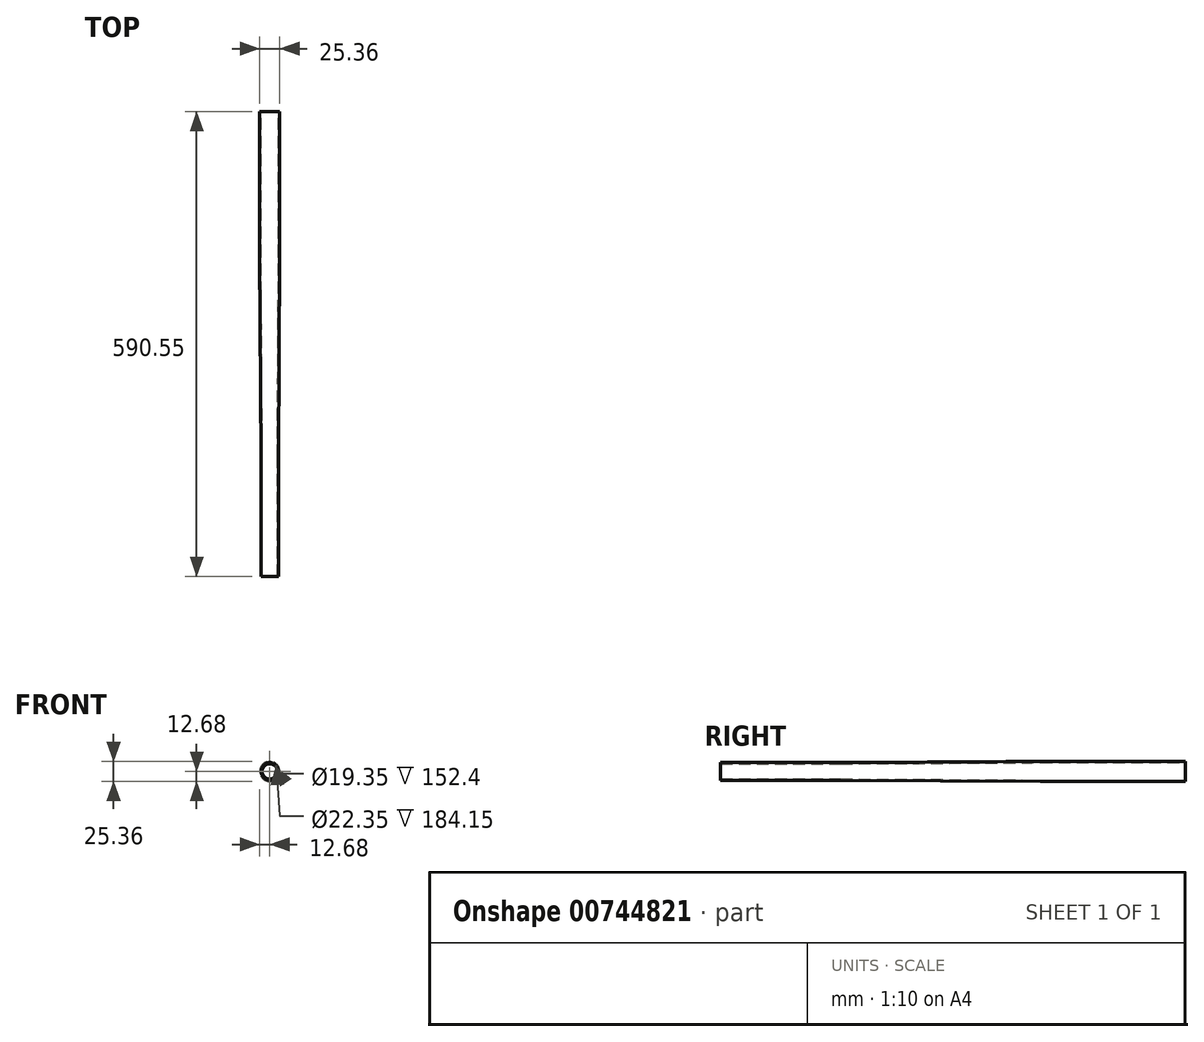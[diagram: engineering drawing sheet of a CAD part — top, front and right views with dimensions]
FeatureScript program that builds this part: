
annotation { "Feature Type Name" : "Feature", "Feature Type Description" : "" }
export const myFeature = defineFeature(function(context is Context, id is Id, definition is map)
    precondition{}
    {
        {
            var Q0;
            Q0=qCreatedBy(makeId("Right.planeOp"),FACE);
            var sketch = newSketch(context, id + "F0", { "sketchPlane" : qUnion([Q0])});
            skLineSegment(sketch, "E0", {"start": v(0, 0) * mm, "end": v(-19.05, 0) * mm});
            skLineSegment(sketch, "E1", {"start": v(-19.05, 0) * mm, "end": v(-184.15, 0) * mm});
            skLineSegment(sketch, "E2", {"start": v(-184.15, 0) * mm, "end": v(-438.15, 0) * mm});
            skLineSegment(sketch, "E3", {"start": v(-438.15, 0) * mm, "end": v(-590.55, 0) * mm});
            skLineSegment(sketch, "E4", {"start": v(0, 12.68) * mm, "end": v(-184.15, 12.68) * mm});
            skLineSegment(sketch, "E5", {"start": v(0, -14.92) * mm, "end": v(-184.15, -14.92) * mm});
            skLineSegment(sketch, "E6", {"start": v(-438.15, 11.18) * mm, "end": v(-590.55, 11.18) * mm});
            skLineSegment(sketch, "E7", {"start": v(-438.15, -11.18) * mm, "end": v(-590.55, -11.18) * mm});
            skLineSegment(sketch, "E8", {"start": v(-184.15, 12.68) * mm, "end": v(-438.15, 11.18) * mm});
            skLineSegment(sketch, "E9", {"start": v(-438.15, -11.18) * mm, "end": v(-184.15, -14.92) * mm});
            skLineSegment(sketch, "E10", {"start": v(-590.55, 11.18) * mm, "end": v(-590.55, 9.68) * mm});
            skLineSegment(sketch, "E11", {"start": v(-590.55, -11.18) * mm, "end": v(-590.55, -9.68) * mm});
            skLineSegment(sketch, "E12", {"start": v(-590.55, -9.68) * mm, "end": v(-438.15, -9.68) * mm});
            skLineSegment(sketch, "E13", {"start": v(-590.55, 9.68) * mm, "end": v(-438.15, 9.68) * mm});
            skLineSegment(sketch, "E14", {"start": v(0, 12.68) * mm, "end": v(0, 11.18) * mm});
            skLineSegment(sketch, "E15", {"start": v(0, -14.92) * mm, "end": v(0, -13.42) * mm});
            skLineSegment(sketch, "E16", {"start": v(0, 11.18) * mm, "end": v(-184.15, 11.18) * mm});
            skLineSegment(sketch, "E17", {"start": v(0, -13.42) * mm, "end": v(-184.15, -13.42) * mm});
            skLineSegment(sketch, "E18", {"start": v(-184.15, 11.18) * mm, "end": v(-438.15, 9.68) * mm});
            skLineSegment(sketch, "E19", {"start": v(-184.15, -13.42) * mm, "end": v(-438.15, -9.68) * mm});
            skSolve(sketch);
        }
        {
            var Q0;
            Q0=makeQuery(id+"F0.imprint","IMPRINT",FACE,{"disambiguationData":[TD([[makeQuery(id+"F0.imprint","IMPRINT",EDGE,{"derivedFrom":sQuery(id+"F0.wireOp",EDGE,"E4")}),1.0]])]});
            var Q1;
            Q1=sQuery(id+"F0.wireOp",EDGE,"E1");
            revolve(context, id + "F1", {"surfaceOperationType" : NewSurfaceOperationType.NEW, "entities" : qUnion([Q0]), "axis" : qUnion([Q1]), "revolveType" : RevolveType.FULL});
        }
    });
